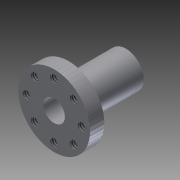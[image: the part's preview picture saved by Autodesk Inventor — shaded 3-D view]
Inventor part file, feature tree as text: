
AUTODESK INVENTOR PART (.ipt)
format: ipt  version: 2015 (Build 190159000, 159)  size: 5,728,768 bytes
history: native  units: in
note: dims shown in document units (in); Inventor stores cm internally (conversion verified against a paired STEP export)
features: thread x8, hole x8, sketch x7, other x3, extrude x2
ambient origin geometry x8: Origin, YZ Plane, XZ Plane, XY Plane, X Axis, Y Axis, Z Axis, Center Point
bodies: Body1 (feature_tree), Body2 (feature_tree), Body3 (feature_tree), Body4 (feature_tree), Body5 (feature_tree), Body6 (feature_tree), Body7 (feature_tree), Body8 (feature_tree), Body9 (feature_tree), Body10 (feature_tree), Body11 (feature_tree), Body12 (feature_tree), Body13 (feature_tree), Body14 (feature_tree), Body15 (feature_tree), Body16 (feature_tree), Body17 (feature_tree), Body18 (feature_tree), Body19 (feature_tree), Body20 (feature_tree), Body21 (feature_tree), Body22 (feature_tree), Body23 (feature_tree), Body24 (feature_tree), Body25 (feature_tree), Body26 (feature_tree), Body27 (feature_tree), Body28 (feature_tree), Body29 (feature_tree), Body30 (feature_tree), Body31 (feature_tree), Body32 (feature_tree), Body33 (feature_tree), Body34 (feature_tree), Body35 (feature_tree), Body36 (feature_tree), Body37 (feature_tree), Body38 (feature_tree), Body39 (feature_tree), Body40 (feature_tree), Body41 (feature_tree), Body42 (feature_tree), Body43 (feature_tree), Body44 (feature_tree), Body45 (feature_tree), Body46 (feature_tree), Body47 (feature_tree), Body48 (feature_tree), Body49 (feature_tree), Body50 (feature_tree), Body51 (feature_tree), Body52 (feature_tree), Body53 (feature_tree), Body54 (feature_tree), Body55 (feature_tree), Body56 (feature_tree), Body57 (feature_tree), Body58 (feature_tree), Body59 (feature_tree), Body60 (feature_tree), Body61 (feature_tree), Body62 (feature_tree), Body63 (feature_tree), Body64 (feature_tree), Body65 (feature_tree), Body66 (feature_tree), Body67 (feature_tree), Body68 (feature_tree), Body69 (feature_tree), Body70 (feature_tree), Body71 (feature_tree), Body72 (feature_tree), Body73 (feature_tree), Body74 (feature_tree), Body75 (feature_tree), Body76 (feature_tree), Body77 (feature_tree), Body78 (feature_tree), Body79 (feature_tree), Body80 (feature_tree), Body81 (feature_tree), Body82 (feature_tree), Body83 (feature_tree), Body84 (feature_tree), Body85 (feature_tree), Body86 (feature_tree), Body87 (feature_tree), Body88 (feature_tree), Body89 (feature_tree), Body90 (feature_tree), Body91 (feature_tree), Body92 (feature_tree), Body93 (feature_tree), Body94 (feature_tree), Body95 (feature_tree), Body96 (feature_tree), Body97 (feature_tree), Body98 (feature_tree), Body99 (feature_tree), Body100 (feature_tree), Body101 (feature_tree), Body102 (feature_tree), Body103 (feature_tree), Body104 (feature_tree), Body105 (feature_tree), Body106 (feature_tree), Body107 (feature_tree), Body108 (feature_tree), Body109 (feature_tree), Body110 (feature_tree), Body111 (feature_tree), Body112 (feature_tree), Body113 (feature_tree), Body114 (feature_tree), Body115 (feature_tree), Body116 (feature_tree), Body117 (feature_tree), Body118 (feature_tree), Body119 (feature_tree), Body120 (feature_tree), Body121 (feature_tree), Body122 (feature_tree), Body123 (feature_tree), Body124 (feature_tree), Body125 (feature_tree), Body126 (feature_tree), Body127 (feature_tree), Body128 (feature_tree), Body129 (feature_tree), Body130 (feature_tree), Body131 (feature_tree), Body132 (feature_tree), Body133 (feature_tree), Body134 (feature_tree), Body135 (feature_tree), Body136 (feature_tree), Body137 (feature_tree), Body138 (feature_tree), Body139 (feature_tree), Body140 (feature_tree), Body141 (feature_tree), Body142 (feature_tree), Body143 (feature_tree), Body144 (feature_tree), Body145 (feature_tree), Body146 (feature_tree), Body147 (feature_tree), Body148 (feature_tree), Body149 (feature_tree), Body150 (feature_tree), Body151 (feature_tree), Body152 (feature_tree), Body153 (feature_tree), Body154 (feature_tree), Body155 (feature_tree), Body156 (feature_tree), Body157 (feature_tree), Body158 (feature_tree), Body159 (feature_tree), Body160 (feature_tree), Body161 (feature_tree), Body162 (feature_tree), Body163 (feature_tree), Body164 (feature_tree), Body165 (feature_tree), Body166 (feature_tree), Body167 (feature_tree), Body168 (feature_tree), Body169 (feature_tree), Body170 (feature_tree), Body171 (feature_tree), Body172 (feature_tree), Body173 (feature_tree), Body174 (feature_tree), Body175 (feature_tree), Body176 (feature_tree), Body177 (feature_tree), Body178 (feature_tree), Body179 (feature_tree), Body180 (feature_tree), Body181 (feature_tree), Body182 (feature_tree), Body183 (feature_tree), Body184 (feature_tree), Body185 (feature_tree), Body186 (feature_tree), Body187 (feature_tree), Body188 (feature_tree), Body189 (feature_tree), Body190 (feature_tree), Body191 (feature_tree), Body192 (feature_tree), Body193 (feature_tree), Body194 (feature_tree), Body195 (feature_tree), Body196 (feature_tree), Body197 (feature_tree), Body198 (feature_tree), Body199 (feature_tree), Body200 (feature_tree), Body201 (feature_tree), Body202 (feature_tree), Body203 (feature_tree), Body204 (feature_tree), Body205 (feature_tree), Body206 (feature_tree), Body207 (feature_tree), Body208 (feature_tree), Body209 (feature_tree), Body210 (feature_tree), Body211 (feature_tree), Body212 (feature_tree), Body213 (feature_tree), Body214 (feature_tree), Body215 (feature_tree), Body216 (feature_tree), Body217 (feature_tree), Body218 (feature_tree), Body219 (feature_tree), Body220 (feature_tree), Body221 (feature_tree), Body222 (feature_tree), Body223 (feature_tree), Body224 (feature_tree), Body225 (feature_tree), Body226 (feature_tree), Body227 (feature_tree), Body228 (feature_tree), Body229 (feature_tree), Body230 (feature_tree), Body231 (feature_tree), Body232 (feature_tree), Body233 (feature_tree), Body234 (feature_tree), Body235 (feature_tree), Body236 (feature_tree), Body237 (feature_tree), Body238 (feature_tree), Body239 (feature_tree), Body240 (feature_tree), Body241 (feature_tree), Body242 (feature_tree), Body243 (feature_tree), Body244 (feature_tree), Body245 (feature_tree), Body246 (feature_tree), Body247 (feature_tree), Body248 (feature_tree), Body249 (feature_tree), Body250 (feature_tree), Body251 (feature_tree), Body252 (feature_tree), Body253 (feature_tree), Body254 (feature_tree), Body255 (feature_tree), Body256 (feature_tree), Body257 (feature_tree), Body258 (feature_tree), Body259 (feature_tree), Body260 (feature_tree), Body261 (feature_tree), Body262 (feature_tree), Body263 (feature_tree), Body264 (feature_tree), Body265 (feature_tree), Body266 (feature_tree), Body267 (feature_tree), Body268 (feature_tree), Body269 (feature_tree), Body270 (feature_tree), Body271 (feature_tree), Body272 (feature_tree), Body273 (feature_tree), Body274 (feature_tree), Body275 (feature_tree), Body276 (feature_tree), Body277 (feature_tree), Body278 (feature_tree), Body279 (feature_tree), Body280 (feature_tree), Body281 (feature_tree), Body282 (feature_tree), Body283 (feature_tree), Body284 (feature_tree), Body285 (feature_tree), Body286 (feature_tree), Body287 (feature_tree), Body288 (feature_tree), Body289 (feature_tree), Body290 (feature_tree), Body291 (feature_tree), Body292 (feature_tree), Body293 (feature_tree), Body294 (feature_tree), Body295 (feature_tree), Body296 (feature_tree), Body297 (feature_tree), Body298 (feature_tree), Body299 (feature_tree), Body300 (feature_tree), Body301 (feature_tree), Body302 (feature_tree), Body303 (feature_tree), Body304 (feature_tree), Body305 (feature_tree), Body306 (feature_tree), Body307 (feature_tree), Body308 (feature_tree), Body309 (feature_tree), Body310 (feature_tree), Body311 (feature_tree), Body312 (feature_tree), Body313 (feature_tree), Body314 (feature_tree), Body315 (feature_tree), Body316 (feature_tree), Body317 (feature_tree), Body318 (feature_tree), Body319 (feature_tree), Body320 (feature_tree), Body321 (feature_tree), Body322 (feature_tree), Body323 (feature_tree), Body324 (feature_tree), Body325 (feature_tree), Body326 (feature_tree), Body327 (feature_tree), Body328 (feature_tree), Body329 (feature_tree), Body330 (feature_tree), Body331 (feature_tree), Body332 (feature_tree), Body333 (feature_tree), Body334 (feature_tree), Body335 (feature_tree), Body336 (feature_tree), Body337 (feature_tree), Body338 (feature_tree), Body339 (feature_tree), Body340 (feature_tree), Body341 (feature_tree), Body342 (feature_tree), Body343 (feature_tree), Body344 (feature_tree), Body345 (feature_tree), Body346 (feature_tree), Body347 (feature_tree), Body348 (feature_tree), Body349 (feature_tree), Body350 (feature_tree), Body351 (feature_tree), Body352 (feature_tree), Body353 (feature_tree), Body354 (feature_tree), Body355 (feature_tree), Body356 (feature_tree), Body357 (feature_tree), Body358 (feature_tree), Body359 (feature_tree), Body360 (feature_tree), Body361 (feature_tree), Body362 (feature_tree), Body363 (feature_tree), Body364 (feature_tree), Body365 (feature_tree), Body366 (feature_tree), Body367 (feature_tree), Body368 (feature_tree), Body369 (feature_tree), Body370 (feature_tree), Body371 (feature_tree), Body372 (feature_tree), Body373 (feature_tree), Body374 (feature_tree), Body375 (feature_tree), Body376 (feature_tree), Body377 (feature_tree), Body378 (feature_tree), Body379 (feature_tree), Body380 (feature_tree), Body381 (feature_tree), Body382 (feature_tree), Body383 (feature_tree), Body384 (feature_tree), Body385 (feature_tree), Body386 (feature_tree), Body387 (feature_tree), Body388 (feature_tree), Body389 (feature_tree), Body390 (feature_tree), Body391 (feature_tree), Body392 (feature_tree), Body393 (feature_tree), Body394 (feature_tree), Body395 (feature_tree), Body396 (feature_tree), Body397 (feature_tree), Body398 (feature_tree), Body399 (feature_tree), Body400 (feature_tree), Body401 (feature_tree), Body402 (feature_tree), Body403 (feature_tree), Body404 (feature_tree), Body405 (feature_tree), Body406 (feature_tree), Body407 (feature_tree), Body408 (feature_tree), Body409 (feature_tree), Body410 (feature_tree), Body411 (feature_tree), Body412 (feature_tree), Body413 (feature_tree), Body414 (feature_tree), Body415 (feature_tree), Body416 (feature_tree), Body417 (feature_tree), Body418 (feature_tree), Body419 (feature_tree), Body420 (feature_tree), Body421 (feature_tree), Body422 (feature_tree), Body423 (feature_tree), Body424 (feature_tree), Body425 (feature_tree), Body426 (feature_tree), Body427 (feature_tree), Body428 (feature_tree), Body429 (feature_tree), Body430 (feature_tree), Body431 (feature_tree), Body432 (feature_tree), Body433 (feature_tree), Body434 (feature_tree), Body435 (feature_tree), Body436 (feature_tree), Body437 (feature_tree), Body438 (feature_tree), Body439 (feature_tree), Body440 (feature_tree), Body441 (feature_tree), Body442 (feature_tree), Body443 (feature_tree), Body444 (feature_tree), Body445 (feature_tree), Body446 (feature_tree), Body447 (feature_tree), Body448 (feature_tree), Body449 (feature_tree), Body450 (feature_tree), Body451 (feature_tree), Body452 (feature_tree), Body453 (feature_tree), Body454 (feature_tree), Body455 (feature_tree), Body456 (feature_tree), Body457 (feature_tree), Body458 (feature_tree), Body459 (feature_tree), Body460 (feature_tree), Body461 (feature_tree), Body462 (feature_tree), Body463 (feature_tree), Body464 (feature_tree), Body465 (feature_tree), Body466 (feature_tree), Body467 (feature_tree), Body468 (feature_tree), Body469 (feature_tree), Body470 (feature_tree), Body471 (feature_tree), Body472 (feature_tree), Body473 (feature_tree), Body474 (feature_tree), Body475 (feature_tree), Body476 (feature_tree), Body477 (feature_tree), Body478 (feature_tree), Body479 (feature_tree), Body480 (feature_tree), Body481 (feature_tree), Body482 (feature_tree), Body483 (feature_tree), Body484 (feature_tree), Body485 (feature_tree), Body486 (feature_tree), Body487 (feature_tree), Body488 (feature_tree), Body489 (feature_tree), Body490 (feature_tree), Body491 (feature_tree), Body492 (feature_tree), Body493 (feature_tree), Body494 (feature_tree), Body495 (feature_tree), Body496 (feature_tree), Body497 (feature_tree), Body498 (feature_tree), Body499 (feature_tree), Body500 (feature_tree), Body501 (feature_tree), Body502 (feature_tree), Body503 (feature_tree), Body504 (feature_tree), Body505 (feature_tree), Body506 (feature_tree), Body507 (feature_tree), Body508 (feature_tree), Body509 (feature_tree), Body510 (feature_tree), Body511 (feature_tree), Body512 (feature_tree), Body513 (feature_tree), Body514 (feature_tree), Body515 (feature_tree), Body516 (feature_tree), Body517 (feature_tree), Body518 (feature_tree), Body519 (feature_tree), Body520 (feature_tree), Body521 (feature_tree), Body522 (feature_tree), Body523 (feature_tree), Body524 (feature_tree), Body525 (feature_tree), Body526 (feature_tree), Body527 (feature_tree), Body528 (feature_tree), Body529 (feature_tree), Body530 (feature_tree), Body531 (feature_tree), Body532 (feature_tree), Body533 (feature_tree), Body534 (feature_tree), Body535 (feature_tree), Body536 (feature_tree), Body537 (feature_tree), Body538 (feature_tree), Body539 (feature_tree), Body540 (feature_tree), Body541 (feature_tree), Body542 (feature_tree), Body543 (feature_tree), Body544 (feature_tree), Body545 (feature_tree), Body546 (feature_tree), Body547 (feature_tree), Body548 (feature_tree), Body549 (feature_tree), Body550 (feature_tree), Body551 (feature_tree), Body552 (feature_tree), Body553 (feature_tree), Body554 (feature_tree), Body555 (feature_tree), Body556 (feature_tree), Body557 (feature_tree), Body558 (feature_tree), Body559 (feature_tree), Body560 (feature_tree), Body561 (feature_tree), Body562 (feature_tree), Body563 (feature_tree), Body564 (feature_tree), Body565 (feature_tree), Body566 (feature_tree), Body567 (feature_tree), Body568 (feature_tree), Body569 (feature_tree), Body570 (feature_tree), Body571 (feature_tree), Body572 (feature_tree), Body573 (feature_tree), Body574 (feature_tree), Body575 (feature_tree), Body576 (feature_tree), Body577 (feature_tree), Body578 (feature_tree), Body579 (feature_tree), Body580 (feature_tree), Body581 (feature_tree), Body582 (feature_tree), Body583 (feature_tree), Body584 (feature_tree), Body585 (feature_tree), Body586 (feature_tree), Body587 (feature_tree), Body588 (feature_tree), Body589 (feature_tree), Body590 (feature_tree), Body591 (feature_tree), Body592 (feature_tree), Body593 (feature_tree), Body594 (feature_tree), Body595 (feature_tree), Body596 (feature_tree), Body597 (feature_tree), Body598 (feature_tree), Body599 (feature_tree), Body600 (feature_tree), Body601 (feature_tree), Body602 (feature_tree), Body603 (feature_tree), Body604 (feature_tree), Body605 (feature_tree), Body606 (feature_tree), Body607 (feature_tree), Body608 (feature_tree), Body609 (feature_tree), Body610 (feature_tree), Body611 (feature_tree), Body612 (feature_tree), Body613 (feature_tree), Body614 (feature_tree), Body615 (feature_tree), Body616 (feature_tree), Body617 (feature_tree), Body618 (feature_tree), Body619 (feature_tree), Body620 (feature_tree), Body621 (feature_tree), Body622 (feature_tree), Body623 (feature_tree), Body624 (feature_tree), Body625 (feature_tree), Body626 (feature_tree), Body627 (feature_tree), Body628 (feature_tree), Body629 (feature_tree), Body630 (feature_tree), Body631 (feature_tree), Body632 (feature_tree), Body633 (feature_tree), Body634 (feature_tree), Body635 (feature_tree), Body636 (feature_tree), Body637 (feature_tree), Body638 (feature_tree), Body639 (feature_tree), Body640 (feature_tree), Body641 (feature_tree), Body642 (feature_tree), Body643 (feature_tree), Body644 (feature_tree), Body645 (feature_tree), Body646 (feature_tree), Body647 (feature_tree), Body648 (feature_tree), Body649 (feature_tree), Body650 (feature_tree), Body651 (feature_tree), Body652 (feature_tree), Body653 (feature_tree), Body654 (feature_tree), Body655 (feature_tree), Body656 (feature_tree), Body657 (feature_tree), Body658 (feature_tree), Body659 (feature_tree), Body660 (feature_tree), Body661 (feature_tree), Body662 (feature_tree), Body663 (feature_tree), Body664 (feature_tree), Body665 (feature_tree), Body666 (feature_tree), Body667 (feature_tree), Body668 (feature_tree), Body669 (feature_tree), Body670 (feature_tree), Body671 (feature_tree), Body672 (feature_tree), Body673 (feature_tree), Body674 (feature_tree), Body675 (feature_tree), Body676 (feature_tree), Body677 (feature_tree), Body678 (feature_tree), Body679 (feature_tree), Body680 (feature_tree), Body681 (feature_tree), Body682 (feature_tree), Body683 (feature_tree), Body684 (feature_tree), Body685 (feature_tree), Body686 (feature_tree), Body687 (feature_tree), Body688 (feature_tree), Body689 (feature_tree), Body690 (feature_tree), Body691 (feature_tree), Body692 (feature_tree), Body693 (feature_tree), Body694 (feature_tree), Body695 (feature_tree), Body696 (feature_tree), Body697 (feature_tree), Body698 (feature_tree), Body699 (feature_tree), Body700 (feature_tree), Body701 (feature_tree), Body702 (feature_tree), Body703 (feature_tree), Body704 (feature_tree), Body705 (feature_tree), Body706 (feature_tree), Body707 (feature_tree), Body708 (feature_tree), Body709 (feature_tree), Body710 (feature_tree), Body711 (feature_tree), Body712 (feature_tree), Body713 (feature_tree), Body714 (feature_tree), Body715 (feature_tree), Body716 (feature_tree), Body717 (feature_tree), Body718 (feature_tree), Body719 (feature_tree), Body720 (feature_tree), Body721 (feature_tree), Body722 (feature_tree), Body723 (feature_tree), Body724 (feature_tree), Body725 (feature_tree), Body726 (feature_tree), Body727 (feature_tree), Body728 (feature_tree), Body729 (feature_tree), Body730 (feature_tree), Body731 (feature_tree), Body732 (feature_tree), Body733 (feature_tree), Body734 (feature_tree), Body735 (feature_tree), Body736 (feature_tree), Body737 (feature_tree), Body738 (feature_tree), Body739 (feature_tree), Body740 (feature_tree), Body741 (feature_tree), Body742 (feature_tree), Body743 (feature_tree), Body744 (feature_tree), Body745 (feature_tree), Body746 (feature_tree), Body747 (feature_tree), Body748 (feature_tree), Body749 (feature_tree), Body750 (feature_tree), Body751 (feature_tree), Body752 (feature_tree), Body753 (feature_tree), Body754 (feature_tree), Body755 (feature_tree), Body756 (feature_tree), Body757 (feature_tree), Body758 (feature_tree), Body759 (feature_tree), Body760 (feature_tree), Body761 (feature_tree), Body762 (feature_tree), Body763 (feature_tree), Body764 (feature_tree), Body765 (feature_tree), Body766 (feature_tree), Body767 (feature_tree), Body768 (feature_tree), Body769 (feature_tree), Body770 (feature_tree), Body771 (feature_tree), Body772 (feature_tree), Body773 (feature_tree), Body774 (feature_tree), Body775 (feature_tree), Body776 (feature_tree), Body777 (feature_tree), Body778 (feature_tree), Body779 (feature_tree), Body780 (feature_tree), Body781 (feature_tree), Body782 (feature_tree), Body783 (feature_tree), Body784 (feature_tree), Body785 (feature_tree), Body786 (feature_tree), Body787 (feature_tree), Body788 (feature_tree), Body789 (feature_tree), Body790 (feature_tree), Body791 (feature_tree), Body792 (feature_tree), Body793 (feature_tree), Body794 (feature_tree), Body795 (feature_tree), Body796 (feature_tree), Body797 (feature_tree), Body798 (feature_tree), Body799 (feature_tree), Body800 (feature_tree), Body801 (feature_tree), Body802 (feature_tree), Body803 (feature_tree), Body804 (feature_tree), Body805 (feature_tree), Body806 (feature_tree), Body807 (feature_tree), Body808 (feature_tree), Body809 (feature_tree), Body810 (feature_tree), Body811 (feature_tree), Body812 (feature_tree), Body813 (feature_tree), Body814 (feature_tree), Body815 (feature_tree), Body816 (feature_tree), Body817 (feature_tree), Body818 (feature_tree), Body819 (feature_tree), Body820 (feature_tree), Body821 (feature_tree), Body822 (feature_tree), Body823 (feature_tree), Body824 (feature_tree), Body825 (feature_tree), Body826 (feature_tree), Body827 (feature_tree), Body828 (feature_tree), Body829 (feature_tree), Body830 (feature_tree), Body831 (feature_tree), Body832 (feature_tree), Body833 (feature_tree), Body834 (feature_tree), Body835 (feature_tree), Body836 (feature_tree), Body837 (feature_tree), Body838 (feature_tree), Body839 (feature_tree), Body840 (feature_tree), Body841 (feature_tree), Body842 (feature_tree), Body843 (feature_tree), Body844 (feature_tree), Body845 (feature_tree), Body846 (feature_tree), Body847 (feature_tree), Body848 (feature_tree), Body849 (feature_tree), Body850 (feature_tree), Body851 (feature_tree), Body852 (feature_tree), Body853 (feature_tree), Body854 (feature_tree), Body855 (feature_tree), Body856 (feature_tree), Body857 (feature_tree), Body858 (feature_tree), Body859 (feature_tree), Body860 (feature_tree), Body861 (feature_tree), Body862 (feature_tree), Body863 (feature_tree), Body864 (feature_tree), Body865 (feature_tree), Body866 (feature_tree), Body867 (feature_tree), Body868 (feature_tree), Body869 (feature_tree), Body870 (feature_tree), Body871 (feature_tree), Body872 (feature_tree), Body873 (feature_tree), Body874 (feature_tree), Body875 (feature_tree), Body876 (feature_tree), Body877 (feature_tree), Body878 (feature_tree), Body879 (feature_tree), Body880 (feature_tree), Body881 (feature_tree), Body882 (feature_tree), Body883 (feature_tree), Body884 (feature_tree), Body885 (feature_tree), Body886 (feature_tree), Body887 (feature_tree), Body888 (feature_tree), Body889 (feature_tree), Body890 (feature_tree), Body891 (feature_tree), Body892 (feature_tree), Body893 (feature_tree), Body894 (feature_tree), Body895 (feature_tree), Body896 (feature_tree), Body897 (feature_tree), Body898 (feature_tree), Body899 (feature_tree), Body900 (feature_tree), Body901 (feature_tree), Body902 (feature_tree), Body903 (feature_tree), Body904 (feature_tree), Body905 (feature_tree), Body906 (feature_tree), Body907 (feature_tree), Body908 (feature_tree), Body909 (feature_tree), Body910 (feature_tree), Body911 (feature_tree), Body912 (feature_tree), Body913 (feature_tree), Body914 (feature_tree), Body915 (feature_tree), Body916 (feature_tree), Body917 (feature_tree), Body918 (feature_tree), Body919 (feature_tree), Body920 (feature_tree), Body921 (feature_tree), Body922 (feature_tree), Body923 (feature_tree), Body924 (feature_tree), Body925 (feature_tree), Body926 (feature_tree), Body927 (feature_tree), Body928 (feature_tree), Body929 (feature_tree), Body930 (feature_tree), Body931 (feature_tree), Body932 (feature_tree), Body933 (feature_tree), Body934 (feature_tree), Body935 (feature_tree), Body936 (feature_tree), Body937 (feature_tree), Body938 (feature_tree), Body939 (feature_tree), Body940 (feature_tree), Body941 (feature_tree), Body942 (feature_tree), Body943 (feature_tree), Body944 (feature_tree), Body945 (feature_tree), Body946 (feature_tree), Body947 (feature_tree), Body948 (feature_tree), Body949 (feature_tree), Body950 (feature_tree), Body951 (feature_tree), Body952 (feature_tree), Body953 (feature_tree), Body954 (feature_tree), Body955 (feature_tree), Body956 (feature_tree), Body957 (feature_tree), Body958 (feature_tree), Body959 (feature_tree), Body960 (feature_tree), Body961 (feature_tree), Body962 (feature_tree), Body963 (feature_tree), Body964 (feature_tree), Body965 (feature_tree), Body966 (feature_tree), Body967 (feature_tree), Body968 (feature_tree), Body969 (feature_tree), Body970 (feature_tree), Body971 (feature_tree), Body972 (feature_tree), Body973 (feature_tree), Body974 (feature_tree), Body975 (feature_tree), Body976 (feature_tree), Body977 (feature_tree), Body978 (feature_tree), Body979 (feature_tree), Body980 (feature_tree), Body981 (feature_tree), Body982 (feature_tree), Body983 (feature_tree), Body984 (feature_tree), Body985 (feature_tree), Body986 (feature_tree), Body987 (feature_tree), Body988 (feature_tree), Body989 (feature_tree), Body990 (feature_tree), Body991 (feature_tree), Body992 (feature_tree), Body993 (feature_tree), Body994 (feature_tree), Body995 (feature_tree), Body996 (feature_tree), Body997 (feature_tree), Body998 (feature_tree), Body999 (feature_tree), Body1000 (feature_tree), Body1001 (feature_tree), Body1002 (feature_tree), Body1003 (feature_tree), Body1004 (feature_tree), Body1005 (feature_tree), Body1006 (feature_tree), Body1007 (feature_tree), Body1008 (feature_tree), Body1009 (feature_tree), Body1010 (feature_tree), Body1011 (feature_tree), Body1012 (feature_tree), Body1013 (feature_tree), Body1014 (feature_tree), Body1015 (feature_tree), Body1016 (feature_tree), Body1017 (feature_tree), Body1018 (feature_tree), Body1019 (feature_tree), Body1020 (feature_tree), Body1021 (feature_tree), Body1022 (feature_tree), Body1023 (feature_tree), Body1024 (feature_tree), Body1025 (feature_tree), Body1026 (feature_tree), Body1027 (feature_tree), Body1028 (feature_tree), Body1029 (feature_tree), Body1030 (feature_tree), Body1031 (feature_tree), Body1032 (feature_tree), Body1033 (feature_tree), Body1034 (feature_tree), Body1035 (feature_tree), Body1036 (feature_tree), Body1037 (feature_tree), Body1038 (feature_tree), Body1039 (feature_tree), Body1040 (feature_tree), Body1041 (feature_tree), Body1042 (feature_tree), Body1043 (feature_tree), Body1044 (feature_tree), Body1045 (feature_tree), Body1046 (feature_tree), Body1047 (feature_tree), Body1048 (feature_tree), Body1049 (feature_tree), Body1050 (feature_tree), Body1051 (feature_tree), Body1052 (feature_tree), Body1053 (feature_tree), Body1054 (feature_tree), Body1055 (feature_tree), Body1056 (feature_tree), Body1057 (feature_tree), Body1058 (feature_tree), Body1059 (feature_tree), Body1060 (feature_tree), Body1061 (feature_tree), Body1062 (feature_tree), Body1063 (feature_tree), Body1064 (feature_tree), Body1065 (feature_tree), Body1066 (feature_tree), Body1067 (feature_tree), Body1068 (feature_tree), Body1069 (feature_tree), Body1070 (feature_tree), Body1071 (feature_tree), Body1072 (feature_tree), Body1073 (feature_tree), Body1074 (feature_tree), Body1075 (feature_tree), Body1076 (feature_tree), Body1077 (feature_tree), Body1078 (feature_tree), Body1079 (feature_tree), Body1080 (feature_tree), Body1081 (feature_tree), Body1082 (feature_tree), Body1083 (feature_tree), Body1084 (feature_tree), Body1085 (feature_tree), Body1086 (feature_tree), Body1087 (feature_tree), Body1088 (feature_tree), Body1089 (feature_tree), Body1090 (feature_tree), Body1091 (feature_tree), Body1092 (feature_tree), Body1093 (feature_tree), Body1094 (feature_tree), Body1095 (feature_tree), Body1096 (feature_tree), Body1097 (feature_tree), Body1098 (feature_tree), Body1099 (feature_tree), Body1100 (feature_tree), Body1101 (feature_tree), Body1102 (feature_tree), Body1103 (feature_tree), Body1104 (feature_tree), Body1105 (feature_tree), Body1106 (feature_tree), Body1107 (feature_tree), Body1108 (feature_tree), Body1109 (feature_tree), Body1110 (feature_tree), Body1111 (feature_tree), Body1112 (feature_tree), Body1113 (feature_tree), Body1114 (feature_tree), Body1115 (feature_tree), Body1116 (feature_tree), Body1117 (feature_tree), Body1118 (feature_tree), Body1119 (feature_tree), Body1120 (feature_tree), Body1121 (feature_tree), Body1122 (feature_tree), Body1123 (feature_tree), Body1124 (feature_tree), Body1125 (feature_tree), Body1126 (feature_tree), Body1127 (feature_tree), Body1128 (feature_tree), Body1129 (feature_tree), Body1130 (feature_tree), Body1131 (feature_tree), Body1132 (feature_tree), Body1133 (feature_tree), Body1134 (feature_tree), Body1135 (feature_tree), Body1136 (feature_tree), Body1137 (feature_tree), Body1138 (feature_tree), Body1139 (feature_tree), Body1140 (feature_tree), Body1141 (feature_tree), Body1142 (feature_tree), Body1143 (feature_tree), Body1144 (feature_tree), Body1145 (feature_tree), Body1146 (feature_tree), Body1147 (feature_tree), Body1148 (feature_tree), Body1149 (feature_tree), Body1150 (feature_tree), Body1151 (feature_tree), Body1152 (feature_tree), Body1153 (feature_tree), Body1154 (feature_tree), Body1155 (feature_tree), Body1156 (feature_tree), Body1157 (feature_tree), Body1158 (feature_tree), Body1159 (feature_tree), Body1160 (feature_tree), Body1161 (feature_tree), Body1162 (feature_tree), Body1163 (feature_tree), Body1164 (feature_tree), Body1165 (feature_tree), Body1166 (feature_tree), Body1167 (feature_tree), Body1168 (feature_tree), Body1169 (feature_tree), Body1170 (feature_tree), Body1171 (feature_tree), Body1172 (feature_tree), Body1173 (feature_tree), Body1174 (feature_tree), Body1175 (feature_tree), Body1176 (feature_tree), Body1177 (feature_tree), Body1178 (feature_tree), Body1179 (feature_tree), Body1180 (feature_tree), Body1181 (feature_tree), Body1182 (feature_tree), Body1183 (feature_tree), Body1184 (feature_tree), Body1185 (feature_tree), Body1186 (feature_tree), Body1187 (feature_tree), Body1188 (feature_tree), Body1189 (feature_tree), Body1190 (feature_tree), Body1191 (feature_tree), Body1192 (feature_tree), Body1193 (feature_tree), Body1194 (feature_tree), Body1195 (feature_tree), Body1196 (feature_tree), Body1197 (feature_tree), Body1198 (feature_tree), Body1199 (feature_tree), Body1200 (feature_tree), Body1201 (feature_tree), Body1202 (feature_tree), Body1203 (feature_tree), Body1204 (feature_tree), Body1205 (feature_tree), Body1206 (feature_tree), Body1207 (feature_tree), Body1208 (feature_tree), Body1209 (feature_tree), Body1210 (feature_tree), Body1211 (feature_tree), Body1212 (feature_tree), Body1213 (feature_tree), Body1214 (feature_tree), Body1215 (feature_tree), Body1216 (feature_tree), Body1217 (feature_tree), Body1218 (feature_tree), Body1219 (feature_tree), Body1220 (feature_tree), Body1221 (feature_tree), Body1222 (feature_tree), Body1223 (feature_tree), Body1224 (feature_tree), Body1225 (feature_tree), Body1226 (feature_tree), Body1227 (feature_tree), Body1228 (feature_tree), Body1229 (feature_tree), Body1230 (feature_tree), Body1231 (feature_tree), Body1232 (feature_tree), Body1233 (feature_tree), Body1234 (feature_tree), Body1235 (feature_tree), Body1236 (feature_tree), Body1237 (feature_tree), Body1238 (feature_tree), Body1239 (feature_tree), Body1240 (feature_tree), Body1241 (feature_tree), Body1242 (feature_tree), Body1243 (feature_tree), Body1244 (feature_tree), Body1245 (feature_tree), Body1246 (feature_tree), Body1247 (feature_tree), Body1248 (feature_tree), Body1249 (feature_tree), Body1250 (feature_tree), Body1251 (feature_tree), Body1252 (feature_tree), Body1253 (feature_tree), Body1254 (feature_tree)
feature tree (28):
  other  "525122.dwg1"
  extrude  "Extrusion2"  TaperAngle=0.0deg  [1 undecoded]
  extrude  "Extrusion3"  Depth=1.0in
  sketch  "Sketch7"  dims[d24=1.0in d25=0.0in d26=1.0in d27=0.0in]
  thread  "Thread1"  [1 undecoded]
  thread  "Thread2"  [1 undecoded]
  thread  "Thread3"  [1 undecoded]
  thread  "Thread4"  [1 undecoded]
  thread  "Thread5"  [1 undecoded]
  thread  "Thread6"  [1 undecoded]
  thread  "Thread7"  [1 undecoded]
  thread  "Thread8"  [1 undecoded]
  hole  "Hole2"  [1 undecoded]
  hole  "Hole4"  [1 undecoded]
  hole  "Hole6"  [1 undecoded]
  hole  "Hole8"  [1 undecoded]
  other  "3D TITLE_BLOCK"
  sketch  "Sketch4"  dims[d2=1.0in d5=0.0in]
  sketch  "Sketch6"  dims[d6=0.0in d8=0.1065in d9=3.1496in d11=360.0deg d13=0.77in d14=0.3in d15=1.0in d16=0.0in d17=0.5in d18=1.0in d19=0.0in d20=1.0in d21=0.0in d22=1.0in d23=0.0in]
  sketch  "Sketch8"  dims[d28=1.0in d29=0.0in d30=1.0in d31=0.0in]
  hole  "Hole1"  [1 undecoded]
  sketch  "Sketch9"  dims[d32=1.0in d33=0.0in d34=1.0in d35=0.0in]
  hole  "Hole3"  [1 undecoded]
  sketch  "Sketch10"  dims[d36=0.104in d37=0.319in d38=0.375in d39=0.25in d40=0.5635in d41=0.388in d42=120.0deg]
  hole  "Hole5"  [1 undecoded]
  sketch  "Sketch11"  dims[d43=0.104in d44=0.319in d45=0.375in d46=0.25in d47=0.5635in d48=0.388in d49=120.0deg d50=0.104in d51=0.319in d52=0.375in d53=0.25in d54=0.5635in d55=0.388in d56=120.0deg d57=0.104in d58=0.319in d59=0.375in d60=0.25in d61=0.5635in d62=0.388in d63=120.0deg]
  hole  "Hole7"  [1 undecoded]
  other  "Srf1"
note: 17 required parameter values undecoded (feature->parameter linkage not recoverable at this tier; creation-order binding heuristic only, values carry confidence <= 0.55)
